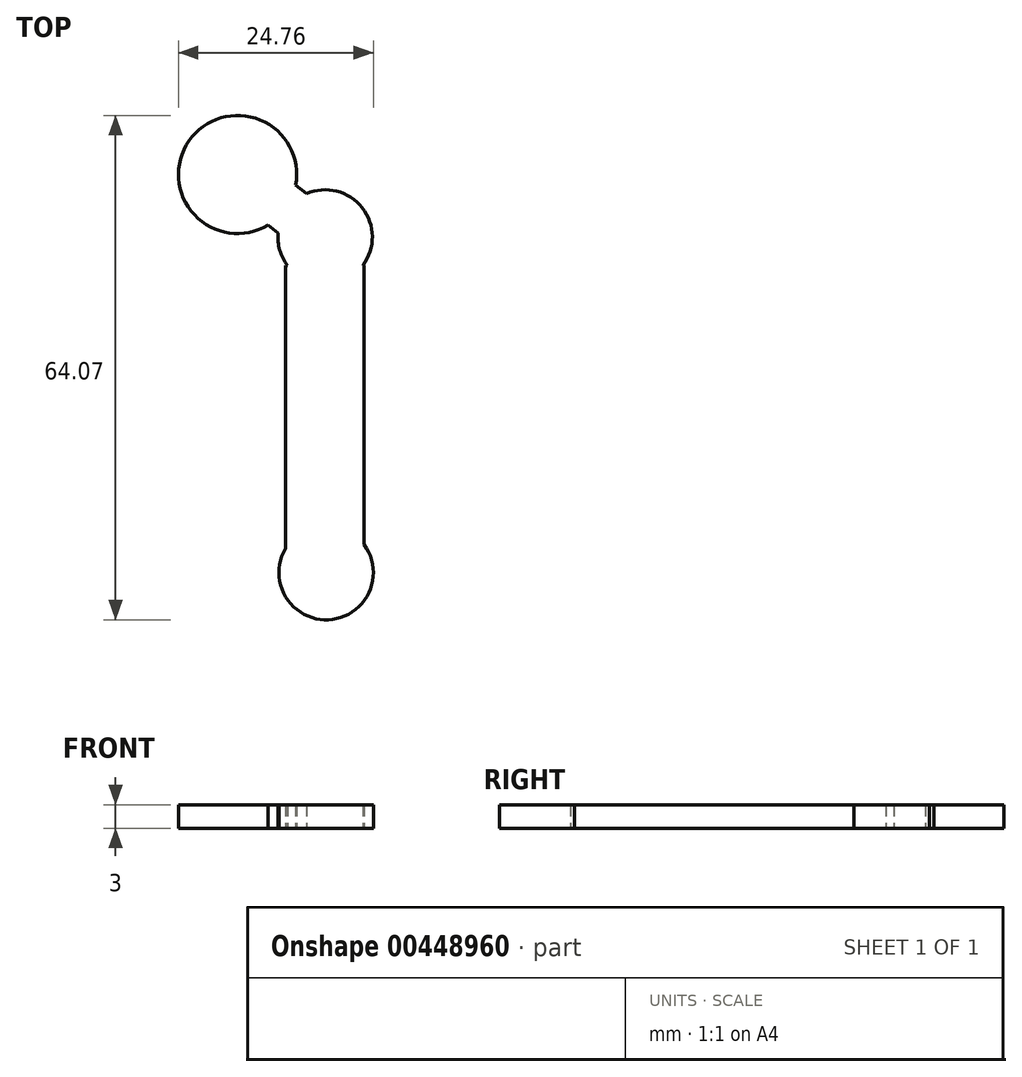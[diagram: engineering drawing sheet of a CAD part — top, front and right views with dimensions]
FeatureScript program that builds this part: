
annotation { "Feature Type Name" : "Feature", "Feature Type Description" : "" }
export const myFeature = defineFeature(function(context is Context, id is Id, definition is map)
    precondition{}
    {
        {
            var Q0;
            Q0=qCreatedBy(makeId("Top.planeOp"),FACE);
            var sketch = newSketch(context, id + "F0", { "sketchPlane" : qUnion([Q0])});
            skLineSegment(sketch, "E0.bottom", {"start": v(0, 0) * mm, "end": v(10, 0) * mm});
            skLineSegment(sketch, "E0.top", {"start": v(0, -36) * mm, "end": v(10, -36) * mm});
            skLineSegment(sketch, "E0.left", {"start": v(0, 0) * mm, "end": v(0, -36) * mm});
            skLineSegment(sketch, "E0.right", {"start": v(10, 0) * mm, "end": v(10, -36) * mm});
            skSolve(sketch);
        }
        {
            var Q0;
            Q0=qCreatedBy(makeId("Top.planeOp"),FACE);
            var sketch = newSketch(context, id + "F1", { "sketchPlane" : qUnion([Q0])});
            skCircle(sketch, "E1", {"center": v(5.03, 3.6) * mm, "radius": 6 * mm});
            skSolve(sketch);
        }
        {
            var Q0;
            Q0=qCreatedBy(makeId("Top.planeOp"),FACE);
            var sketch = newSketch(context, id + "F2", { "sketchPlane" : qUnion([Q0])});
            skCircle(sketch, "E2", {"center": v(5.16, -39.02) * mm, "radius": 6 * mm});
            skSolve(sketch);
        }
        {
            var Q0;
            Q0=makeQuery(id+"F0.imprint","IMPRINT",FACE,{"disambiguationData":[TD([[makeQuery(id+"F0.imprint","IMPRINT",EDGE,{"derivedFrom":sQuery(id+"F0.wireOp",EDGE,"E0.bottom")}),-1.0]])]});
            extrude(context, id + "F3", {"entities" : qUnion([Q0]), "depth" : 3 * mm});
        }
        {
            var Q0;
            Q0=makeQuery(id+"F2.imprint","IMPRINT",FACE,{"disambiguationData":[TD([[makeQuery(id+"F2.imprint","IMPRINT",EDGE,{"derivedFrom":sQuery(id+"F2.wireOp",EDGE,"E2")}),1.0]])]});
            extrude(context, id + "F4", {"entities" : qUnion([Q0]), "operationType" : NewBodyOperationType.ADD, "depth" : 3 * mm});
        }
        {
            var Q0;
            Q0=makeQuery(id+"F1.imprint","IMPRINT",FACE,{"disambiguationData":[TD([[makeQuery(id+"F1.imprint","IMPRINT",EDGE,{"derivedFrom":sQuery(id+"F1.wireOp",EDGE,"E1")}),1.0]])]});
            extrude(context, id + "F5", {"entities" : qUnion([Q0]), "operationType" : NewBodyOperationType.ADD, "depth" : 3 * mm});
        }
        {
            var Q0;
            Q0=qCreatedBy(makeId("Top.planeOp"),FACE);
            var sketch = newSketch(context, id + "F6", { "sketchPlane" : qUnion([Q0])});
            skLineSegment(sketch, "E3", {"start": v(2.87, 8.93) * mm, "end": v(-0.96, 4.1) * mm});
            skLineSegment(sketch, "E4", {"start": v(-0.96, 4.1) * mm, "end": v(-2.96, 5.68) * mm});
            skLineSegment(sketch, "E5", {"start": v(2.87, 8.93) * mm, "end": v(1.05, 10.37) * mm});
            skLineSegment(sketch, "E6", {"start": v(1.05, 10.37) * mm, "end": v(-2.96, 5.68) * mm});
            skSolve(sketch);
        }
        {
            var Q0;
            Q0=qCreatedBy(makeId("Top.planeOp"),FACE);
            var sketch = newSketch(context, id + "F7", { "sketchPlane" : qUnion([Q0])});
            skCircle(sketch, "E7", {"center": v(-6.1, 11.55) * mm, "radius": 7.5 * mm});
            skSolve(sketch);
        }
        {
            var Q0;
            Q0=qCreatedBy(makeId("Top.planeOp"),FACE);
            var sketch = newSketch(context, id + "F8", { "sketchPlane" : qUnion([Q0])});
            skLineSegment(sketch, "E8", {"start": v(-6.09, 11.55) * mm, "end": v(-9.48, 23.67) * mm});
            skLineSegment(sketch, "E9", {"start": v(-9.48, 23.67) * mm, "end": v(-6.09, 11.55) * mm});
            skLineSegment(sketch, "E10", {"start": v(-6.09, 11.55) * mm, "end": v(-19.6, 13.95) * mm});
            skLineSegment(sketch, "E11", {"start": v(-9.48, 23.67) * mm, "end": v(-19.6, 13.95) * mm});
            skSolve(sketch);
        }
        {
            var Q0;
            Q0=makeQuery(id+"F7.imprint","IMPRINT",FACE,{"disambiguationData":[TD([[makeQuery(id+"F7.imprint","IMPRINT",EDGE,{"derivedFrom":sQuery(id+"F7.wireOp",EDGE,"E7")}),1.0]])]});
            extrude(context, id + "F9", {"entities" : qUnion([Q0]), "depth" : 3 * mm});
        }
        {
            var Q0;
            Q0=makeQuery(id+"F6.imprint","IMPRINT",FACE,{"disambiguationData":[TD([[makeQuery(id+"F6.imprint","IMPRINT",EDGE,{"derivedFrom":sQuery(id+"F6.wireOp",EDGE,"E3")}),-1.0]])]});
            extrude(context, id + "F10", {"entities" : qUnion([Q0]), "depth" : 3 * mm});
        }
        {
            var Q0;
            Q0=makeQuery(id+"F9.opExtrude","SWEPT_BODY",BODY,{"disambiguationData":[OSD([sQuery(id+"F7.wireOp",EDGE,"E7")])]});
            var Q1;
            Q1=makeQuery(id+"F3.opExtrude","SWEPT_BODY",BODY,{"disambiguationData":[OSD([sQuery(id+"F0.wireOp",EDGE,"E0.bottom"),sQuery(id+"F0.wireOp",EDGE,"E0.top"),sQuery(id+"F0.wireOp",EDGE,"E0.left"),sQuery(id+"F0.wireOp",EDGE,"E0.right")])]});
            var Q2;
            Q2=makeQuery(id+"F10.opExtrude","SWEPT_BODY",BODY,{"disambiguationData":[OSD([sQuery(id+"F6.wireOp",EDGE,"E3"),sQuery(id+"F6.wireOp",EDGE,"E4"),sQuery(id+"F6.wireOp",EDGE,"E5"),sQuery(id+"F6.wireOp",EDGE,"E6")])]});
            booleanBodies(context, id + "F11", {"operationType" : BooleanOperationType.UNION, "tools" : qUnion([Q0, Q1, Q2])});
        }
        {
            var Q0;
            Q0=makeQuery(id+"F11.opBoolean","MERGE",FACE,{"derivedFrom":[makeQuery(id+"F5.boolean.opBoolean","MERGE",FACE,{"derivedFrom":[makeQuery(id+"F4.boolean.opBoolean","MERGE",FACE,{"derivedFrom":[makeQuery(id+"F3.opExtrude","CAP_FACE",FACE,{"disambiguationData":[OSD([sQuery(id+"F0.wireOp",EDGE,"E0.bottom"),sQuery(id+"F0.wireOp",EDGE,"E0.top"),sQuery(id+"F0.wireOp",EDGE,"E0.left"),sQuery(id+"F0.wireOp",EDGE,"E0.right")])],"isStart":true}),makeQuery(id+"F4.opExtrude","CAP_FACE",FACE,{"disambiguationData":[OSD([sQuery(id+"F2.wireOp",EDGE,"E2")])],"isStart":true})]}),makeQuery(id+"F5.opExtrude","CAP_FACE",FACE,{"disambiguationData":[OSD([sQuery(id+"F1.wireOp",EDGE,"E1")])],"isStart":true})]}),makeQuery(id+"F9.opExtrude","CAP_FACE",FACE,{"disambiguationData":[OSD([sQuery(id+"F7.wireOp",EDGE,"E7")])],"isStart":true}),makeQuery(id+"F10.opExtrude","CAP_FACE",FACE,{"disambiguationData":[OSD([sQuery(id+"F6.wireOp",EDGE,"E3"),sQuery(id+"F6.wireOp",EDGE,"E4"),sQuery(id+"F6.wireOp",EDGE,"E5"),sQuery(id+"F6.wireOp",EDGE,"E6")])],"isStart":true})]});
            var sketch = newSketch(context, id + "F12", { "sketchPlane" : qUnion([Q0])});
            skCircle(sketch, "E12", {"center": v(-6.1, -11.55) * mm, "radius": 3.54 * mm});
            skSolve(sketch);
        }
        {
            var Q0;
            Q0=makeQuery(id+"F8.imprint","IMPRINT",FACE,{"disambiguationData":[TD([[makeQuery(id+"F8.imprint","IMPRINT",EDGE,{"derivedFrom":sQuery(id+"F8.wireOp",EDGE,"E9")}),-1.0]])]});
            var Q1;
            Q1=makeQuery(id+"F12.imprint","IMPRINT",FACE,{"disambiguationData":[TD([[makeQuery(id+"F12.imprint","IMPRINT",EDGE,{"derivedFrom":sQuery(id+"F12.wireOp",EDGE,"E12")}),1.0]])]});
            extrude(context, id + "F13", {"entities" : qUnion([Q0, Q1]), "operationType" : NewBodyOperationType.REMOVE, "depth" : 25 * mm});
        }
    });
